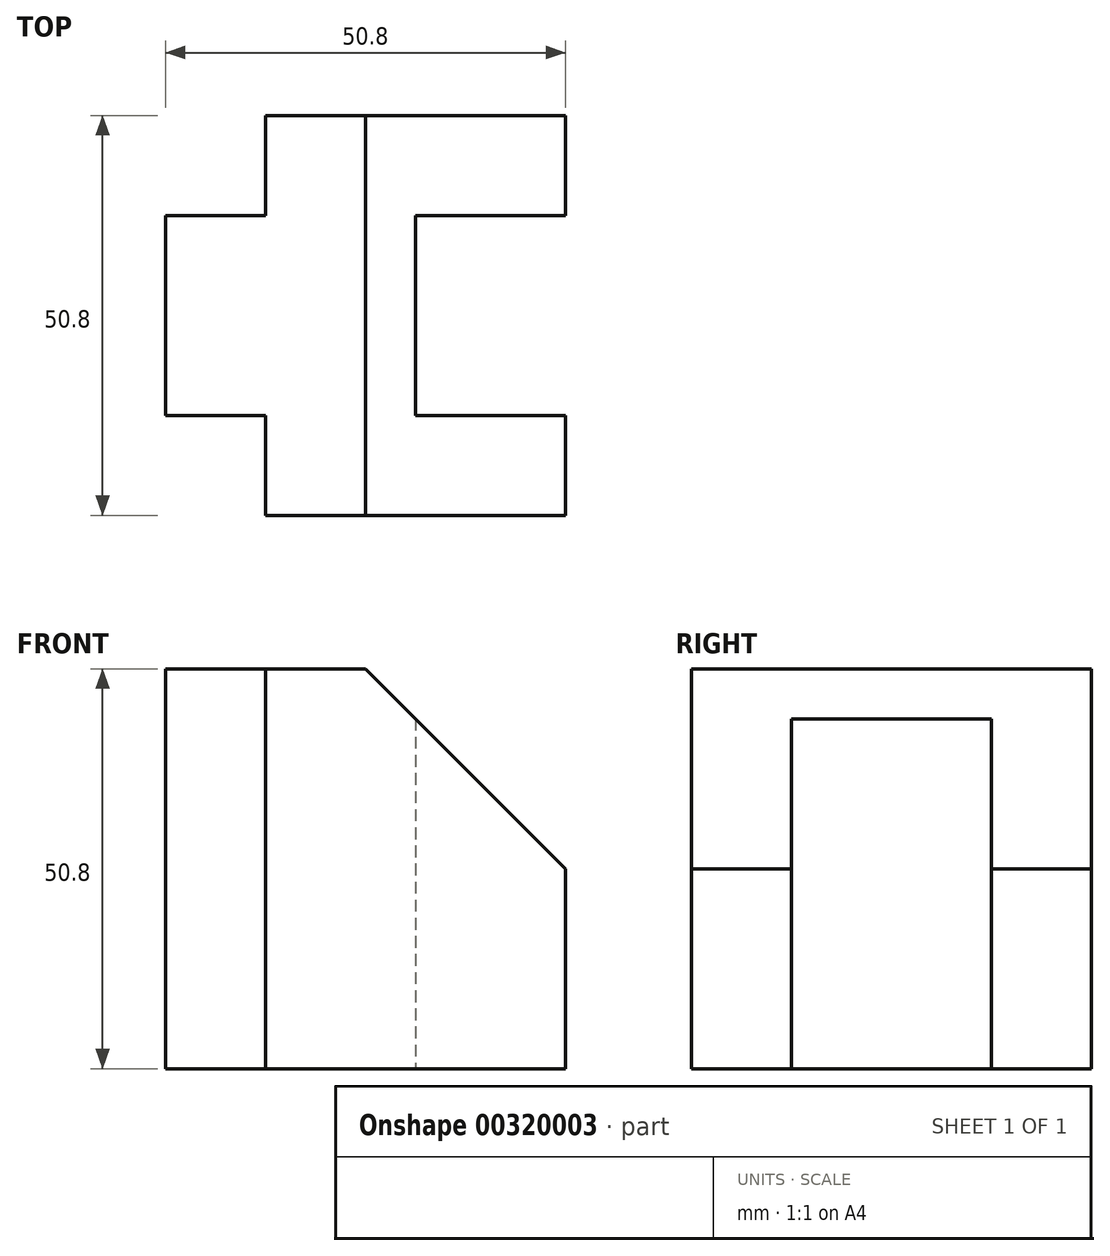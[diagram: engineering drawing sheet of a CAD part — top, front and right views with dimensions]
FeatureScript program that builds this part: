
annotation { "Feature Type Name" : "Feature", "Feature Type Description" : "" }
export const myFeature = defineFeature(function(context is Context, id is Id, definition is map)
    precondition{}
    {
        {
            var Q0;
            Q0=qCreatedBy(makeId("Front.planeOp"),FACE);
            var sketch = newSketch(context, id + "F0", { "sketchPlane" : qUnion([Q0])});
            skLineSegment(sketch, "E0.bottom", {"start": v(0, 0) * mm, "end": v(50.8, 0) * mm});
            skLineSegment(sketch, "E0.top", {"start": v(0, 50.8) * mm, "end": v(50.8, 50.8) * mm});
            skLineSegment(sketch, "E0.left", {"start": v(0, 0) * mm, "end": v(0, 50.8) * mm});
            skLineSegment(sketch, "E0.right", {"start": v(50.8, 0) * mm, "end": v(50.8, 50.8) * mm});
            skSolve(sketch);
        }
        {
            var Q0;
            Q0 = qSketchRegion(id + "F0", true);
            extrude(context, id + "F1", {"entities" : qUnion([Q0]), "oppositeDirection" : true, "depth" : 50.8 * mm});
        }
        {
            var Q0;
            Q0=makeQuery(id+"F1.opExtrude","CAP_FACE",FACE,{"disambiguationData":[OSD([sQuery(id+"F0.wireOp",EDGE,"E0.bottom"),sQuery(id+"F0.wireOp",EDGE,"E0.top"),sQuery(id+"F0.wireOp",EDGE,"E0.left"),sQuery(id+"F0.wireOp",EDGE,"E0.right")])],"isStart":true});
            var sketch = newSketch(context, id + "F2", { "sketchPlane" : qUnion([Q0])});
            skLineSegment(sketch, "E1", {"start": v(25.4, 50.8) * mm, "end": v(50.8, 50.8) * mm});
            skLineSegment(sketch, "E2", {"start": v(50.8, 50.8) * mm, "end": v(50.8, 25.4) * mm});
            skLineSegment(sketch, "E3", {"start": v(50.8, 25.4) * mm, "end": v(25.4, 50.8) * mm});
            skSolve(sketch);
        }
        {
            var Q0;
            Q0 = qSketchRegion(id + "F2", true);
            extrude(context, id + "F3", {"entities" : qUnion([Q0]), "operationType" : NewBodyOperationType.REMOVE, "endBound" : BoundingType.THROUGH_ALL, "oppositeDirection" : true, "depth" : 25.4 * mm});
        }
        {
            var Q0;
            Q0=makeQuery(id+"F1.opExtrude","SWEPT_FACE",FACE,{"disambiguationData":[OSD([sQuery(id+"F0.wireOp",EDGE,"E0.top")])]});
            var sketch = newSketch(context, id + "F4", { "sketchPlane" : qUnion([Q0])});
            skLineSegment(sketch, "E4.bottom", {"start": v(0, 0) * mm, "end": v(12.7, 0) * mm});
            skLineSegment(sketch, "E4.top", {"start": v(0, 12.7) * mm, "end": v(12.7, 12.7) * mm});
            skLineSegment(sketch, "E4.left", {"start": v(0, 0) * mm, "end": v(0, 12.7) * mm});
            skLineSegment(sketch, "E4.right", {"start": v(12.7, 0) * mm, "end": v(12.7, 12.7) * mm});
            skLineSegment(sketch, "E5.bottom", {"start": v(0, 50.8) * mm, "end": v(12.7, 50.8) * mm});
            skLineSegment(sketch, "E5.top", {"start": v(0, 38.1) * mm, "end": v(12.7, 38.1) * mm});
            skLineSegment(sketch, "E5.left", {"start": v(0, 50.8) * mm, "end": v(0, 38.1) * mm});
            skLineSegment(sketch, "E5.right", {"start": v(12.7, 50.8) * mm, "end": v(12.7, 38.1) * mm});
            skSolve(sketch);
        }
        {
            var Q0;
            Q0 = qSketchRegion(id + "F4", true);
            extrude(context, id + "F5", {"entities" : qUnion([Q0]), "operationType" : NewBodyOperationType.REMOVE, "endBound" : BoundingType.THROUGH_ALL, "oppositeDirection" : true, "depth" : 25.4 * mm});
        }
        {
            var Q0;
            Q0=makeQuery(id+"F1.opExtrude","SWEPT_FACE",FACE,{"disambiguationData":[OSD([sQuery(id+"F0.wireOp",EDGE,"E0.bottom")])]});
            var sketch = newSketch(context, id + "F6", { "sketchPlane" : qUnion([Q0])});
            skLineSegment(sketch, "E6.bottom", {"start": v(31.75, -12.7) * mm, "end": v(50.8, -12.7) * mm});
            skLineSegment(sketch, "E6.top", {"start": v(31.75, -38.1) * mm, "end": v(50.8, -38.1) * mm});
            skLineSegment(sketch, "E6.left", {"start": v(31.75, -12.7) * mm, "end": v(31.75, -38.1) * mm});
            skLineSegment(sketch, "E6.right", {"start": v(50.8, -12.7) * mm, "end": v(50.8, -38.1) * mm});
            skSolve(sketch);
        }
        {
            var Q0;
            Q0 = qSketchRegion(id + "F6", true);
            extrude(context, id + "F7", {"entities" : qUnion([Q0]), "operationType" : NewBodyOperationType.REMOVE, "endBound" : BoundingType.THROUGH_ALL, "oppositeDirection" : true, "depth" : 25.4 * mm});
        }
    });
